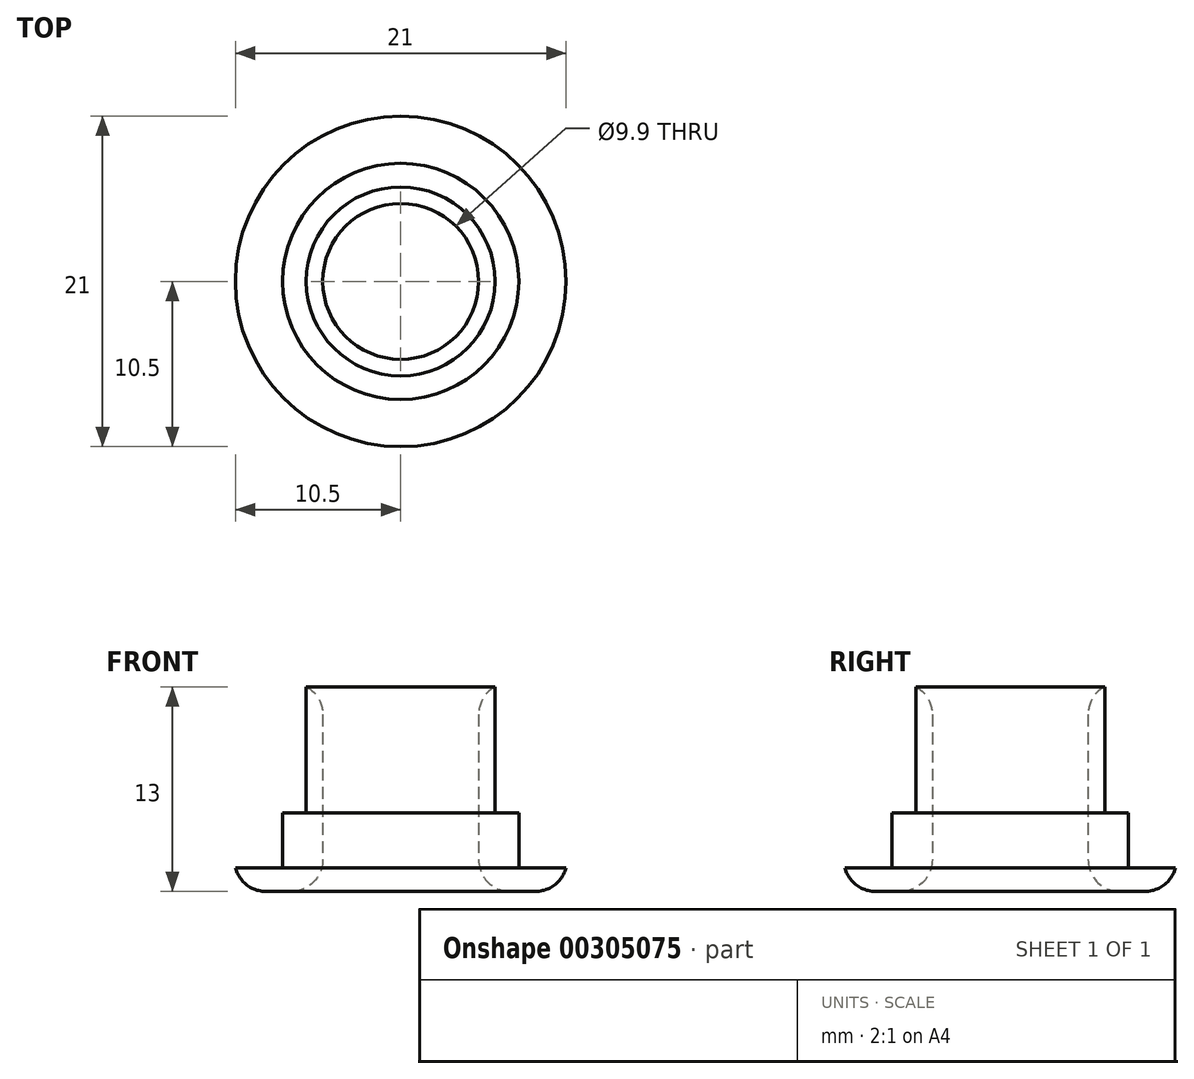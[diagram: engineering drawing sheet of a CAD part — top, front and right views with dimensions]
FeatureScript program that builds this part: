
annotation { "Feature Type Name" : "Feature", "Feature Type Description" : "" }
export const myFeature = defineFeature(function(context is Context, id is Id, definition is map)
    precondition{}
    {
        {
            var Q0;
            Q0=qCreatedBy(makeId("Top.planeOp"),FACE);
            var sketch = newSketch(context, id + "F0", { "sketchPlane" : qUnion([Q0])});
            skCircle(sketch, "E0", {"center": v(0, 0) * mm, "radius": 7.5 * mm});
            skCircle(sketch, "E1", {"center": v(0, 0) * mm, "radius": 10.5 * mm});
            skCircle(sketch, "E2", {"center": v(0, 0) * mm, "radius": 4.95 * mm});
            skSolve(sketch);
        }
        {
            var Q0;
            Q0=makeQuery(id+"F0.imprint","IMPRINT",FACE,{"disambiguationData":[TD([[makeQuery(id+"F0.imprint","IMPRINT",EDGE,{"derivedFrom":sQuery(id+"F0.wireOp",EDGE,"E0")}),-1.0]])]});
            extrude(context, id + "F1", {"entities" : qUnion([Q0]), "offsetDistance" : 25 * mm, "depth" : 1.5 * mm});
        }
        {
            var Q0;
            Q0=makeQuery(id+"F0.imprint","IMPRINT",FACE,{"disambiguationData":[TD([[makeQuery(id+"F0.imprint","IMPRINT",EDGE,{"derivedFrom":sQuery(id+"F0.wireOp",EDGE,"E0")}),1.0]])]});
            var Q1;
            Q1=makeQuery(id+"F0.imprint","IMPRINT",FACE,{"disambiguationData":[TD([[makeQuery(id+"F0.imprint","IMPRINT",EDGE,{"derivedFrom":sQuery(id+"F0.wireOp",EDGE,"NJdIa3up-pmiV-ufMs-v9WN-zdTClBqndQI6")}),1.0]])]});
            extrude(context, id + "F2", {"entities" : qUnion([Q0, Q1]), "operationType" : NewBodyOperationType.ADD, "offsetDistance" : 25 * mm, "depth" : 13 * mm});
        }
        {
            var Q0;
            Q0=makeQuery(id+"F1.opExtrude","CAP_EDGE",EDGE,{"disambiguationData":[OSD([sQuery(id+"F0.wireOp",EDGE,"E1")])],"isStart":true});
            fillet(context, id + "F3", {"entities" : qUnion([Q0]), "radius" : 2 * mm, "tangentPropagation" : true, "allowEdgeOverflow" : false});
        }
        {
            var Q0;
            Q0=makeQuery(id+"F2.opExtrude","CAP_FACE",FACE,{"disambiguationData":[OSD([sQuery(id+"F0.wireOp",EDGE,"E0"),sQuery(id+"F0.wireOp",EDGE,"E2")])],"isStart":false});
            var sketch = newSketch(context, id + "F4", { "sketchPlane" : qUnion([Q0])});
            skCircle(sketch, "E3", {"center": v(0, 0) * mm, "radius": 6 * mm});
            skSolve(sketch);
        }
        {
            var Q0;
            Q0=makeQuery(id+"F4.imprint","IMPRINT",FACE,{"disambiguationData":[TD([[makeQuery(id+"F4.imprint","IMPRINT",EDGE,{"derivedFrom":sQuery(id+"F4.wireOp",EDGE,"E3")}),-1.0]])]});
            extrude(context, id + "F5", {"entities" : qUnion([Q0]), "operationType" : NewBodyOperationType.REMOVE, "oppositeDirection" : true, "offsetDistance" : 25 * mm, "depth" : 8 * mm});
        }
        {
            var Q0;
            Q0=makeQuery(id+"F2.opExtrude","CAP_EDGE",EDGE,{"disambiguationData":[OSD([sQuery(id+"F0.wireOp",EDGE,"E2")])],"isStart":true});
            var Q1;
            Q1=makeQuery(id+"F2.opExtrude","CAP_EDGE",EDGE,{"disambiguationData":[OSD([sQuery(id+"F0.wireOp",EDGE,"E2")])],"isStart":false});
            fillet(context, id + "F6", {"entities" : qUnion([Q0, Q1]), "radius" : 2 * mm, "tangentPropagation" : true, "allowEdgeOverflow" : false});
        }
    });
